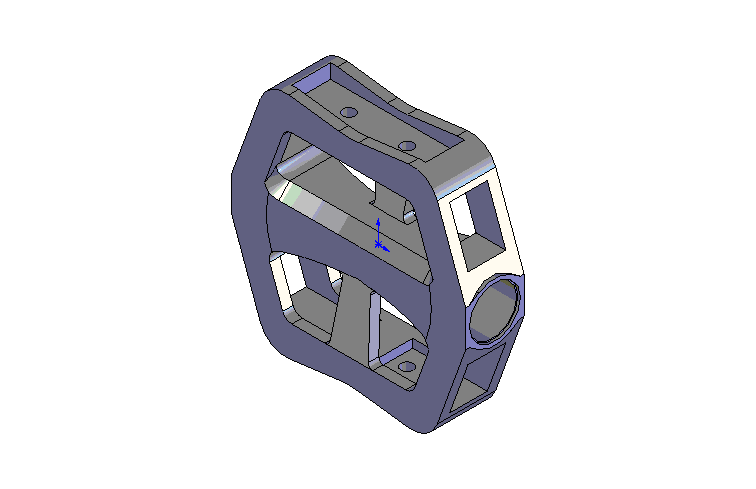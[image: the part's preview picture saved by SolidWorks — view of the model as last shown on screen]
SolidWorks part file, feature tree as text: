
SOLIDWORKS PART (.sldprt)
format: sldprt  version: not decoded by parser v0  size: 1,084,928 bytes
history: native  units: mm
features: sketch x13, cut_extrude x7, extrude x4, plane x3, cut_revolve x2, material x1, fillet x1, chamfer x1, mirror x1 (+10 scaffold rows collapsed)
feature tree (43):
  scaffold x10  (default folders/planes/origin — collapsed)
  material  "Matériau <non spécifié>"
  plane  "Plan de face"
  plane  "Plan de dessus"
  plane  "Plan de droite"
  sketch  "Esquisse1"  dims[c1.D1=11.0mm c1.D6=32.0mm c1.D7=32.0mm c1.D10=155.0mm c1.D11=155.0mm c1.D12=4.0mm c1.D2=52.0mm c1.D3=72.0mm c1.D4=96.0mm c2.D6=~7.777638deg c2.D5=15.0mm c2.D7=88.0mm c2.D8=11.5mm c2.D9=68.0mm c2.D11=17.0mm]
  extrude  "Extrusion1"  Depth=24mm
  sketch  "Esquisse2"  dims[D1=15.5mm D2=21.0mm D3=33.0mm]
  cut_extrude  "Enlèv. mat.-Extru.1"  [1 undecoded]
  sketch  "Esquisse4"  dims[D1=13.0mm]
  extrude  "Extrusion2"  [1 undecoded]
  sketch  "Esquisse5"  dims[D1=155.0mm D2=16.5mm]
  cut_revolve  "Enlèvement de matière-Révolution1"  Angle=360deg
  sketch  "Esquisse9"  dims[D1=3.6mm]
  extrude  "Extrusion4"  Depth=16mm
  sketch  "Esquisse7"  dims[D1=55.0mm D2=7.0mm]
  cut_extrude  "Enlèv. mat.-Extru.2"  Depth=16mm
  sketch  "Esquisse10"  dims[D1=11.0mm]
  cut_extrude  "Enlèv. mat.-Extru.3"  [1 undecoded]
  fillet  "Congé1"  Radius=2mm
  chamfer  "Chanfrein2"  Distance=5mm Angle=45deg
  sketch  "Esquisse11"  dims[c1.D2=12.0mm c1.D3=12.0mm c1.D1=13.0mm c2.D3=24.0mm]
  extrude  "Extrusion5"  [1 undecoded]
  mirror  "Symétrie1"
  sketch  "Esquisse13"  dims[D1=10.0mm]
  cut_extrude  "Enlèv. mat.-Extru.4"  [1 undecoded]
  sketch  "Esquisse14"  dims[c1.D1=~4.070333mm c1.D2=5.0mm c2.D1=24.0mm]
  cut_extrude  "Enlèv. mat.-Extru.5"  [1 undecoded]
  sketch  "Esquisse15"
  cut_extrude  "Enlèv. mat.-Extru.6"  [1 undecoded]
  sketch  "Esquisse16"  dims[D1=12.0mm]
  cut_extrude  "Enlèv. mat.-Extru.7"  [1 undecoded]
  sketch  "Esquisse17"  dims[c1.D2=1.5mm c1.D1=13.5mm c2.D2=~9.59318mm c2.D3=20.0mm c2.D4=6.0mm c2.D5=71.3mm c2.D6=21.0mm c2.D7=1.0mm]
  cut_revolve  "Enlèvement de matière-Révolution2"  Angle=360deg
decode coverage: 19 of 29 modeling features carry decoded parameters
note: ~ marks probable driven/reference dimensions
note: 8 parameter values undecoded
summary: no parameter record found for 8 features
note: suppression state not decoded; provenance and decode notes live in map.json
